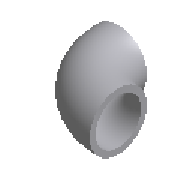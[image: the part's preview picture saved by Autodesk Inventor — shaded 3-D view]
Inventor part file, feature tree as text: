
AUTODESK INVENTOR PART (.ipt)
format: ipt  version: 2024.2 (Build 282272000, 272)  size: 190,976 bytes
history: native  units: mm (DEFAULTED — no unit token found)
features: other x4, sweep x1
ambient origin geometry x8: Origin, YZ Plane, XZ Plane, XY Plane, X Axis, Y Axis, Z Axis, Center Point
bodies: Solid1 (feature_tree)
feature tree (5):
  sweep  "Sweep1"
  other  "Work Point1"
  other  "Work Axis1"
  other  "Work Point2"
  other  "Work Axis2"
